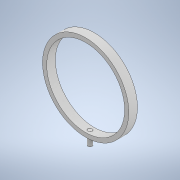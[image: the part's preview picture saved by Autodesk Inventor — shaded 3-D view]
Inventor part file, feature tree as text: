
AUTODESK INVENTOR PART (.ipt)
format: ipt  version: 2022 (Build 260153000, 153)  size: 135,680 bytes
history: native  units: in
note: dims shown in document units (in); Inventor stores cm internally (conversion verified against a paired STEP export)
features: sketch x5, extrude x4, revolve x1
ambient origin geometry x8: Origin, YZ Plane, XZ Plane, XY Plane, X Axis, Y Axis, Z Axis, Center Point
bodies: Solid1 (feature_tree)
feature tree (10):
  sketch  "Sketch1"  dims[d0=1.25in d2=90.0deg]
  sketch  "Sketch2"  dims[d3=0.25in d4=0.0in d5=2.25in]
  revolve  "Revolution1"  Angle=90.0deg
  extrude  "Extrusion1"  Depth=2.25in
  extrude  "Extrusion2"  Depth=0.125in
  extrude  "Extrusion3"  Depth=1.125in TaperAngle=0.0deg
  extrude  "Extrusion4"  [1 undecoded]
  sketch  "Sketch3"  dims[d6=0.25in d7=0.0in d8=0.125in]
  sketch  "Sketch5"  dims[d9=1.5in d10=0.0in d11=1.125in d12=0.0in]
  sketch  "Sketch6"
note: 1 required parameter value undecoded (feature->parameter linkage not recoverable at this tier; creation-order binding heuristic only, values carry confidence <= 0.55)
